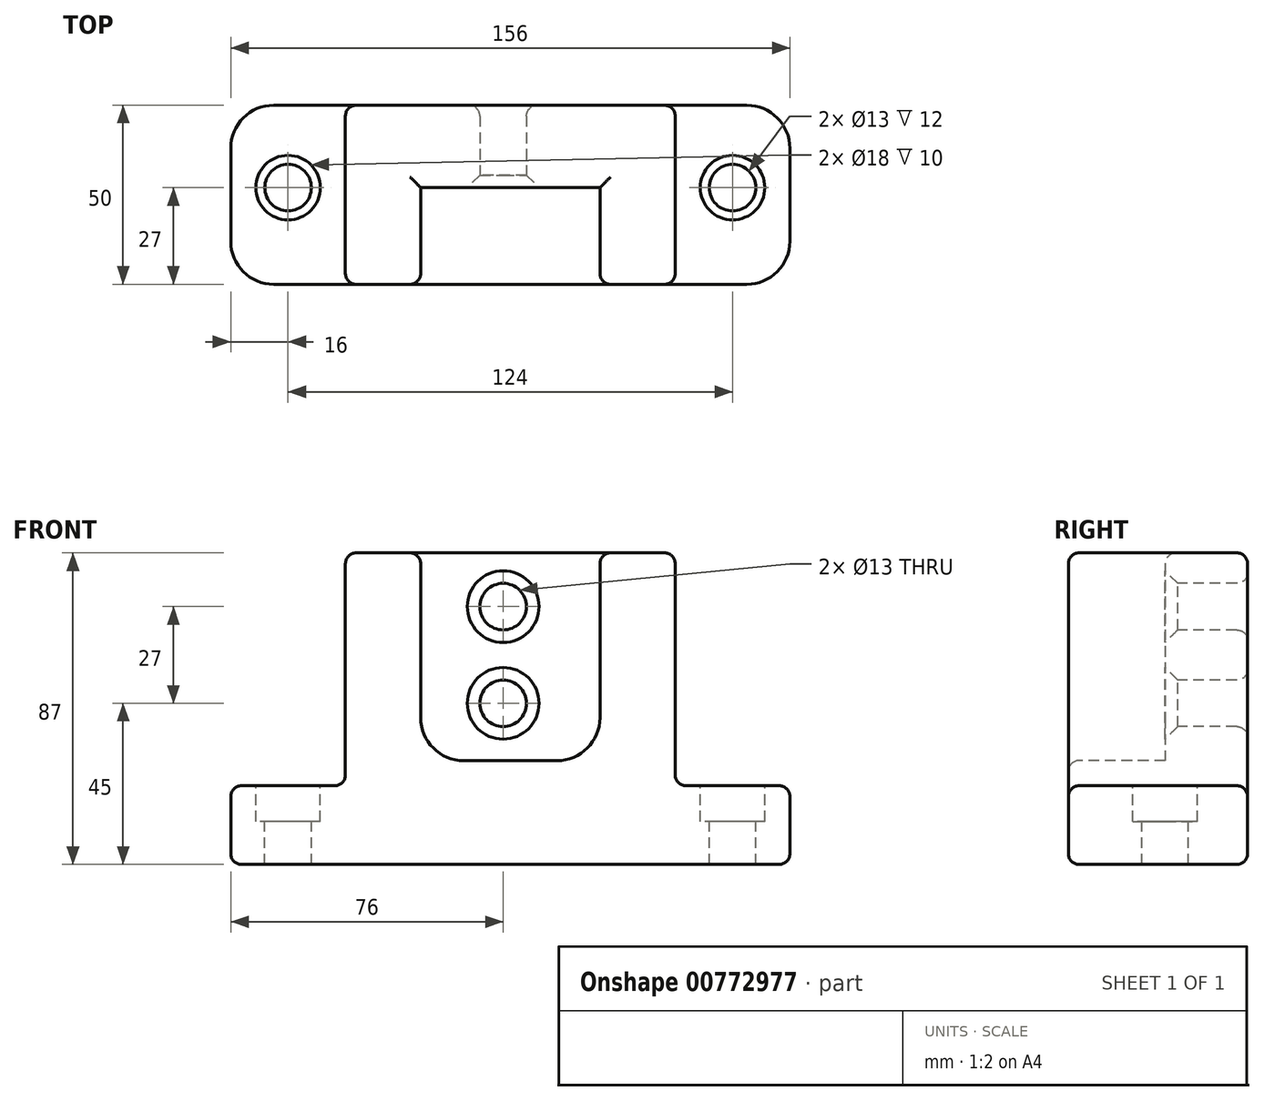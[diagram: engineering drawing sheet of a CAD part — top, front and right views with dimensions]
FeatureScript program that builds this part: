
annotation { "Feature Type Name" : "Feature", "Feature Type Description" : "" }
export const myFeature = defineFeature(function(context is Context, id is Id, definition is map)
    precondition{}
    {
        {
            var Q0;
            Q0=qCreatedBy(makeId("Top.planeOp"),FACE);
            var sketch = newSketch(context, id + "F0", { "sketchPlane" : qUnion([Q0])});
            skLineSegment(sketch, "E0.bottom", {"start": v(0, 0) * mm, "end": v(156, 0) * mm});
            skLineSegment(sketch, "E0.top", {"start": v(0, 50) * mm, "end": v(156, 50) * mm});
            skLineSegment(sketch, "E0.left", {"start": v(0, 0) * mm, "end": v(0, 50) * mm});
            skLineSegment(sketch, "E0.right", {"start": v(156, 0) * mm, "end": v(156, 50) * mm});
            skSolve(sketch);
        }
        {
            var Q0;
            Q0=makeQuery(id+"F0.imprint","IMPRINT",FACE,{"disambiguationData":[TD([[makeQuery(id+"F0.imprint","IMPRINT",EDGE,{"derivedFrom":sQuery(id+"F0.wireOp",EDGE,"E0.bottom")}),1.0]])]});
            extrude(context, id + "F1", {"entities" : qUnion([Q0]), "depth" : 87 * mm, "offsetDistance" : 25 * mm});
        }
        {
            var Q0;
            Q0=makeQuery(id+"F1.opExtrude","SWEPT_FACE",FACE,{"disambiguationData":[OSD([sQuery(id+"F0.wireOp",EDGE,"E0.bottom")])]});
            var sketch = newSketch(context, id + "F2", { "sketchPlane" : qUnion([Q0])});
            skLineSegment(sketch, "E1.bottom", {"start": v(0, 87) * mm, "end": v(32, 87) * mm});
            skLineSegment(sketch, "E1.top", {"start": v(0, 22) * mm, "end": v(32, 22) * mm});
            skLineSegment(sketch, "E1.left", {"start": v(0, 87) * mm, "end": v(0, 22) * mm});
            skLineSegment(sketch, "E1.right", {"start": v(32, 87) * mm, "end": v(32, 22) * mm});
            skLineSegment(sketch, "E2.bottom", {"start": v(156, 87) * mm, "end": v(124, 87) * mm});
            skLineSegment(sketch, "E2.top", {"start": v(156, 22) * mm, "end": v(124, 22) * mm});
            skLineSegment(sketch, "E2.left", {"start": v(156, 87) * mm, "end": v(156, 22) * mm});
            skLineSegment(sketch, "E2.right", {"start": v(124, 87) * mm, "end": v(124, 22) * mm});
            skSolve(sketch);
        }
        {
            var Q0;
            Q0=makeQuery(id+"F2.imprint","IMPRINT",FACE,{"disambiguationData":[TD([[makeQuery(id+"F2.imprint","IMPRINT",EDGE,{"derivedFrom":sQuery(id+"F2.wireOp",EDGE,"E1.bottom")}),-1.0]])]});
            var Q1;
            Q1=makeQuery(id+"F2.imprint","IMPRINT",FACE,{"disambiguationData":[TD([[makeQuery(id+"F2.imprint","IMPRINT",EDGE,{"derivedFrom":sQuery(id+"F2.wireOp",EDGE,"E2.bottom")}),-1.0]])]});
            extrude(context, id + "F3", {"entities" : qUnion([Q0, Q1]), "operationType" : NewBodyOperationType.REMOVE, "endBound" : BoundingType.UP_TO_NEXT, "oppositeDirection" : true, "depth" : mm, "offsetDistance" : 25 * mm});
        }
        {
            var Q0;
            Q0=makeQuery(id+"F1.opExtrude","SWEPT_FACE",FACE,{"disambiguationData":[OSD([sQuery(id+"F0.wireOp",EDGE,"E0.bottom")])]});
            var sketch = newSketch(context, id + "F4", { "sketchPlane" : qUnion([Q0])});
            skLineSegment(sketch, "E3.bottom", {"start": v(53, 87) * mm, "end": v(103, 87) * mm});
            skLineSegment(sketch, "E3.top", {"start": v(53, 29) * mm, "end": v(103, 29) * mm});
            skLineSegment(sketch, "E3.left", {"start": v(53, 87) * mm, "end": v(53, 29) * mm});
            skLineSegment(sketch, "E3.right", {"start": v(103, 87) * mm, "end": v(103, 29) * mm});
            skSolve(sketch);
        }
        {
            var Q0;
            Q0=makeQuery(id+"F4.imprint","IMPRINT",FACE,{"disambiguationData":[TD([[makeQuery(id+"F4.imprint","IMPRINT",EDGE,{"derivedFrom":sQuery(id+"F4.wireOp",EDGE,"E3.bottom")}),-1.0]])]});
            extrude(context, id + "F5", {"entities" : qUnion([Q0]), "operationType" : NewBodyOperationType.REMOVE, "oppositeDirection" : true, "depth" : 27 * mm, "offsetDistance" : 25 * mm});
        }
        {
            var Q0;
            Q0=makeQuery(id+"F3.boolean.opBoolean","COPY",FACE,{"derivedFrom":makeQuery(id+"F3.opExtrude","SWEPT_FACE",FACE,{"disambiguationData":[OSD([sQuery(id+"F2.wireOp",EDGE,"E2.top")])]})});
            var sketch = newSketch(context, id + "F6", { "sketchPlane" : qUnion([Q0])});
            skPoint(sketch, "E4", {"position": v(16, 27) * mm});
            skPoint(sketch, "E5", {"position": v(140, 27) * mm});
            skSolve(sketch);
        }
        {
            var Q0;
            Q0=sQuery(id+"F6.wireOp",VERTEX,"E4");
            var Q1;
            Q1=sQuery(id+"F6.wireOp",VERTEX,"E5");
            var Q2;
            Q2=makeQuery(id+"F1.opExtrude","SWEPT_BODY",BODY,{"disambiguationData":[OSD([sQuery(id+"F0.wireOp",EDGE,"E0.bottom"),sQuery(id+"F0.wireOp",EDGE,"E0.top"),sQuery(id+"F0.wireOp",EDGE,"E0.left"),sQuery(id+"F0.wireOp",EDGE,"E0.right")])]});
            hole(context, id + "F7", {"style" : HoleStyle.C_BORE, "endStyle" : HoleEndStyle.THROUGH, "holeDiameter" : 13 * mm, "cBoreDiameter" : 18 * mm, "cBoreDepth" : 10 * mm, "majorDiameter" : 5 * mm, "isTappedThrough" : true, "tappedDepth" : 12 * mm, "tapClearance" : 3, "locations" : qUnion([Q0, Q1]), "scope" : qUnion([Q2])});
        }
        {
            var Q0;
            Q0=makeQuery(id+"F5.boolean.opBoolean","COPY",FACE,{"derivedFrom":makeQuery(id+"F5.opExtrude","CAP_FACE",FACE,{"disambiguationData":[OSD([sQuery(id+"F4.wireOp",EDGE,"E3.bottom"),sQuery(id+"F4.wireOp",EDGE,"E3.top"),sQuery(id+"F4.wireOp",EDGE,"E3.left"),sQuery(id+"F4.wireOp",EDGE,"E3.right")])],"isStart":false})});
            var sketch = newSketch(context, id + "F8", { "sketchPlane" : qUnion([Q0])});
            skPoint(sketch, "E6", {"position": v(76, 72) * mm});
            skPoint(sketch, "E7", {"position": v(76, 45) * mm});
            skSolve(sketch);
        }
        {
            var Q0;
            Q0=sQuery(id+"F8.wireOp",VERTEX,"E6");
            var Q1;
            Q1=sQuery(id+"F8.wireOp",VERTEX,"E7");
            var Q2;
            Q2=makeQuery(id+"F1.opExtrude","SWEPT_BODY",BODY,{"disambiguationData":[OSD([sQuery(id+"F0.wireOp",EDGE,"E0.bottom"),sQuery(id+"F0.wireOp",EDGE,"E0.top"),sQuery(id+"F0.wireOp",EDGE,"E0.left"),sQuery(id+"F0.wireOp",EDGE,"E0.right")])]});
            hole(context, id + "F9", {"style" : HoleStyle.C_SINK, "endStyle" : HoleEndStyle.THROUGH, "holeDiameter" : 13 * mm, "cSinkDiameter" : 20 * mm, "cSinkAngle" : 90 * degree, "majorDiameter" : 5 * mm, "isTappedThrough" : true, "tappedDepth" : 12 * mm, "tapClearance" : 3, "locations" : qUnion([Q0, Q1]), "scope" : qUnion([Q2])});
        }
        {
            var Q0;
            Q0=makeQuery(id+"F5.boolean.opBoolean","COPY",EDGE,{"derivedFrom":makeQuery(id+"F5.opExtrude","SWEPT_EDGE",EDGE,{"disambiguationData":[OSD([sQuery(id+"F4.wireOp",EDGE,"E3.top"),sQuery(id+"F4.wireOp",EDGE,"E3.left")])]})});
            var Q1;
            Q1=makeQuery(id+"F5.boolean.opBoolean","COPY",EDGE,{"derivedFrom":makeQuery(id+"F5.opExtrude","SWEPT_EDGE",EDGE,{"disambiguationData":[OSD([sQuery(id+"F4.wireOp",EDGE,"E3.top"),sQuery(id+"F4.wireOp",EDGE,"E3.right")])]})});
            var Q2;
            Q2=makeQuery(id+"F1.opExtrude","SWEPT_EDGE",EDGE,{"disambiguationData":[OSD([sQuery(id+"F0.wireOp",EDGE,"E0.bottom"),sQuery(id+"F0.wireOp",EDGE,"E0.left")])]});
            var Q3;
            Q3=makeQuery(id+"F1.opExtrude","SWEPT_EDGE",EDGE,{"disambiguationData":[OSD([sQuery(id+"F0.wireOp",EDGE,"E0.top"),sQuery(id+"F0.wireOp",EDGE,"E0.left")])]});
            var Q4;
            Q4=makeQuery(id+"F1.opExtrude","SWEPT_EDGE",EDGE,{"disambiguationData":[OSD([sQuery(id+"F0.wireOp",EDGE,"E0.bottom"),sQuery(id+"F0.wireOp",EDGE,"E0.right")])]});
            var Q5;
            Q5=makeQuery(id+"F1.opExtrude","SWEPT_EDGE",EDGE,{"disambiguationData":[OSD([sQuery(id+"F0.wireOp",EDGE,"E0.top"),sQuery(id+"F0.wireOp",EDGE,"E0.right")])]});
            fillet(context, id + "F10", {"entities" : qUnion([Q0, Q1, Q2, Q3, Q4, Q5]), "radius" : 12 * mm, "tangentPropagation" : true, "allowEdgeOverflow" : false});
        }
        {
            var Q0;
            Q0=makeQuery(id+"F1.opExtrude","SWEPT_FACE",FACE,{"disambiguationData":[OSD([sQuery(id+"F0.wireOp",EDGE,"E0.bottom")])]});
            var Q1;
            Q1=makeQuery(id+"F3.boolean.opBoolean","COPY",FACE,{"derivedFrom":makeQuery(id+"F3.opExtrude","SWEPT_FACE",FACE,{"disambiguationData":[OSD([sQuery(id+"F2.wireOp",EDGE,"E2.right")])]})});
            var Q2;
            Q2=makeQuery(id+"F1.opExtrude","CAP_FACE",FACE,{"disambiguationData":[OSD([sQuery(id+"F0.wireOp",EDGE,"E0.bottom"),sQuery(id+"F0.wireOp",EDGE,"E0.top"),sQuery(id+"F0.wireOp",EDGE,"E0.left"),sQuery(id+"F0.wireOp",EDGE,"E0.right")])],"isStart":false});
            var Q3;
            Q3=makeQuery(id+"F1.opExtrude","SWEPT_FACE",FACE,{"disambiguationData":[OSD([sQuery(id+"F0.wireOp",EDGE,"E0.top")])]});
            var Q4;
            Q4=makeQuery(id+"F3.boolean.opBoolean","COPY",FACE,{"derivedFrom":makeQuery(id+"F3.opExtrude","SWEPT_FACE",FACE,{"disambiguationData":[OSD([sQuery(id+"F2.wireOp",EDGE,"E1.right")])]})});
            fillet(context, id + "F11", {"entities" : qUnion([Q0, Q1, Q2, Q3, Q4]), "radius" : 3 * mm, "tangentPropagation" : true, "allowEdgeOverflow" : false});
        }
    });
